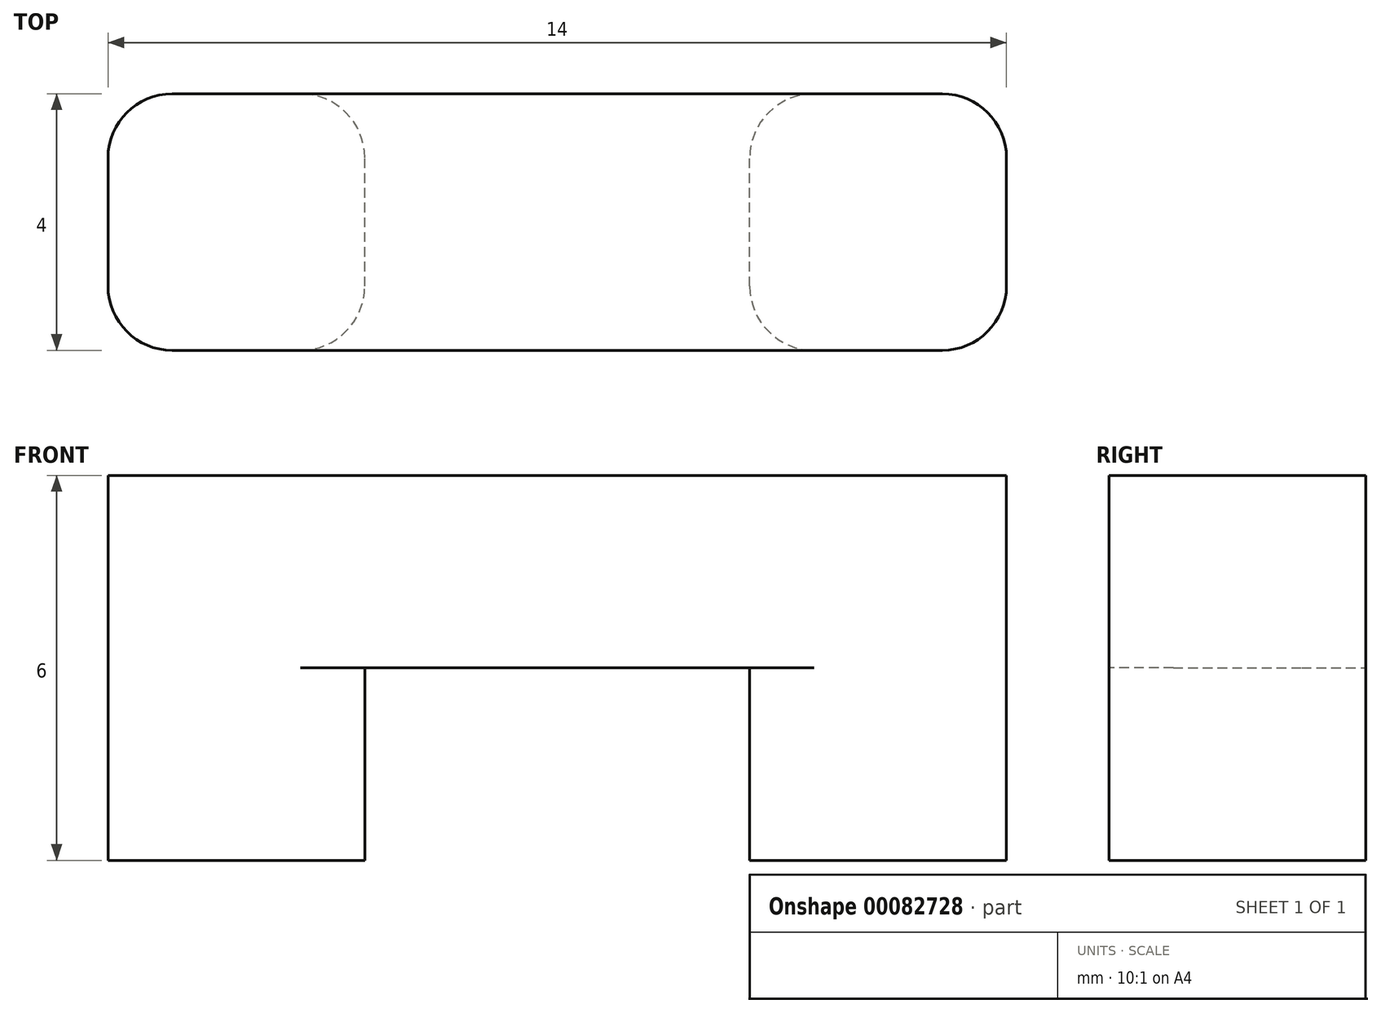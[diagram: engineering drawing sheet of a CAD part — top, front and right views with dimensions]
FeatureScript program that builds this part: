
annotation { "Feature Type Name" : "Feature", "Feature Type Description" : "" }
export const myFeature = defineFeature(function(context is Context, id is Id, definition is map)
    precondition{}
    {
        {
            var Q0;
            Q0=qCreatedBy(makeId("Top.planeOp"),FACE);
            var sketch = newSketch(context, id + "F0", { "sketchPlane" : qUnion([Q0])});
            skLineSegment(sketch, "E0.bottom", {"start": v(3, -2) * mm, "end": v(7, -2) * mm});
            skLineSegment(sketch, "E0.top", {"start": v(3, 2) * mm, "end": v(7, 2) * mm});
            skLineSegment(sketch, "E0.left", {"start": v(3, -2) * mm, "end": v(3, 2) * mm});
            skLineSegment(sketch, "E0.right", {"start": v(7, -2) * mm, "end": v(7, 2) * mm});
            skLineSegment(sketch, "E1.bottom", {"start": v(-7, 2) * mm, "end": v(-3, 2) * mm});
            skLineSegment(sketch, "E1.top", {"start": v(-7, -2) * mm, "end": v(-3, -2) * mm});
            skLineSegment(sketch, "E1.left", {"start": v(-7, -2) * mm, "end": v(-7, 2) * mm});
            skLineSegment(sketch, "E1.right", {"start": v(-3, -2) * mm, "end": v(-3, 2) * mm});
            skLineSegment(sketch, "E2", {"start": v(-7, 0) * mm, "end": v(7, 0) * mm, "construction": true});
            skSolve(sketch);
        }
        {
            var Q0;
            Q0=makeQuery(id+"F0.imprint","IMPRINT",FACE,{"disambiguationData":[TD([[makeQuery(id+"F0.imprint","IMPRINT",EDGE,{"derivedFrom":sQuery(id+"F0.wireOp",EDGE,"E1.bottom")}),-1.0]])]});
            var Q1;
            Q1=makeQuery(id+"F0.imprint","IMPRINT",FACE,{"disambiguationData":[TD([[makeQuery(id+"F0.imprint","IMPRINT",EDGE,{"derivedFrom":sQuery(id+"F0.wireOp",EDGE,"E0.bottom")}),1.0]])]});
            extrude(context, id + "F1", {"entities" : qUnion([Q0, Q1]), "depth" : 3 * mm});
        }
        {
            var Q0;
            Q0=makeQuery(id+"F1.opExtrude","CAP_FACE",FACE,{"disambiguationData":[OSD([sQuery(id+"F0.wireOp",EDGE,"E1.bottom"),sQuery(id+"F0.wireOp",EDGE,"E1.top"),sQuery(id+"F0.wireOp",EDGE,"E1.left"),sQuery(id+"F0.wireOp",EDGE,"E1.right")])],"isStart":false});
            var sketch = newSketch(context, id + "F2", { "sketchPlane" : qUnion([Q0])});
            skLineSegment(sketch, "E3", {"start": v(-7, -2) * mm, "end": v(7, -2) * mm});
            skLineSegment(sketch, "E4", {"start": v(-7, 2) * mm, "end": v(7, 2) * mm});
            skLineSegment(sketch, "E5", {"start": v(-7, -2) * mm, "end": v(-7, 2) * mm});
            skLineSegment(sketch, "E6", {"start": v(7, -2) * mm, "end": v(7, 2) * mm});
            skSolve(sketch);
        }
        {
            var Q0;
            {var subQ0=sQuery(id+"F2.wireOp",EDGE,"E5");Q0=makeQuery(id+"F2.imprint","IMPRINT",FACE,{"disambiguationData":[TD([[makeQuery(id+"F2.imprint","IMPRINT",EDGE,{"derivedFrom":subQ0}),-1.0]])]});}
            var Q1;
            {var subQ2=sQuery(id+"F2.wireOp",EDGE,"E6");Q1=makeQuery(id+"F2.imprint","IMPRINT",FACE,{"disambiguationData":[TD([[makeQuery(id+"F2.imprint","IMPRINT",EDGE,{"derivedFrom":subQ2}),1.0]])]});}
            extrude(context, id + "F3", {"entities" : qUnion([Q0, Q1]), "operationType" : NewBodyOperationType.ADD, "depth" : 3 * mm});
        }
        {
            var Q0;
            Q0=makeQuery(id+"F3.boolean.opBoolean","MERGE",EDGE,{"derivedFrom":[makeQuery(id+"F1.opExtrude","SWEPT_EDGE",EDGE,{"disambiguationData":[OSD([sQuery(id+"F0.wireOp",EDGE,"E1.top"),sQuery(id+"F0.wireOp",EDGE,"E1.left")])]}),makeQuery(id+"F3.opExtrude","SWEPT_EDGE",EDGE,{"disambiguationData":[OSD([sQuery(id+"F2.wireOp",EDGE,"E3"),sQuery(id+"F2.wireOp",EDGE,"E5")])]})]});
            var Q1;
            Q1=makeQuery(id+"F1.opExtrude","SWEPT_EDGE",EDGE,{"disambiguationData":[OSD([sQuery(id+"F0.wireOp",EDGE,"E1.top"),sQuery(id+"F0.wireOp",EDGE,"E1.right")])]});
            var Q2;
            Q2=makeQuery(id+"F1.opExtrude","SWEPT_EDGE",EDGE,{"disambiguationData":[OSD([sQuery(id+"F0.wireOp",EDGE,"E1.bottom"),sQuery(id+"F0.wireOp",EDGE,"E1.right")])]});
            var Q3;
            Q3=makeQuery(id+"F1.opExtrude","SWEPT_EDGE",EDGE,{"disambiguationData":[OSD([sQuery(id+"F0.wireOp",EDGE,"E0.bottom"),sQuery(id+"F0.wireOp",EDGE,"E0.left")])]});
            var Q4;
            Q4=makeQuery(id+"F3.boolean.opBoolean","MERGE",EDGE,{"derivedFrom":[makeQuery(id+"F1.opExtrude","SWEPT_EDGE",EDGE,{"disambiguationData":[OSD([sQuery(id+"F0.wireOp",EDGE,"E0.bottom"),sQuery(id+"F0.wireOp",EDGE,"E0.right")])]}),makeQuery(id+"F3.opExtrude","SWEPT_EDGE",EDGE,{"disambiguationData":[OSD([sQuery(id+"F2.wireOp",EDGE,"E3"),sQuery(id+"F2.wireOp",EDGE,"E6")])]})]});
            var Q5;
            Q5=makeQuery(id+"F3.boolean.opBoolean","MERGE",EDGE,{"derivedFrom":[makeQuery(id+"F1.opExtrude","SWEPT_EDGE",EDGE,{"disambiguationData":[OSD([sQuery(id+"F0.wireOp",EDGE,"E0.top"),sQuery(id+"F0.wireOp",EDGE,"E0.right")])]}),makeQuery(id+"F3.opExtrude","SWEPT_EDGE",EDGE,{"disambiguationData":[OSD([sQuery(id+"F2.wireOp",EDGE,"E4"),sQuery(id+"F2.wireOp",EDGE,"E6")])]})]});
            var Q6;
            Q6=makeQuery(id+"F1.opExtrude","SWEPT_EDGE",EDGE,{"disambiguationData":[OSD([sQuery(id+"F0.wireOp",EDGE,"E0.top"),sQuery(id+"F0.wireOp",EDGE,"E0.left")])]});
            var Q7;
            Q7=makeQuery(id+"F3.boolean.opBoolean","MERGE",EDGE,{"derivedFrom":[makeQuery(id+"F1.opExtrude","SWEPT_EDGE",EDGE,{"disambiguationData":[OSD([sQuery(id+"F0.wireOp",EDGE,"E1.bottom"),sQuery(id+"F0.wireOp",EDGE,"E1.left")])]}),makeQuery(id+"F3.opExtrude","SWEPT_EDGE",EDGE,{"disambiguationData":[OSD([sQuery(id+"F2.wireOp",EDGE,"E4"),sQuery(id+"F2.wireOp",EDGE,"E5")])]})]});
            fillet(context, id + "F4", {"entities" : qUnion([Q0, Q1, Q2, Q3, Q4, Q5, Q6, Q7]), "radius" : 1 * mm, "tangentPropagation" : true, "allowEdgeOverflow" : false});
        }
    });
